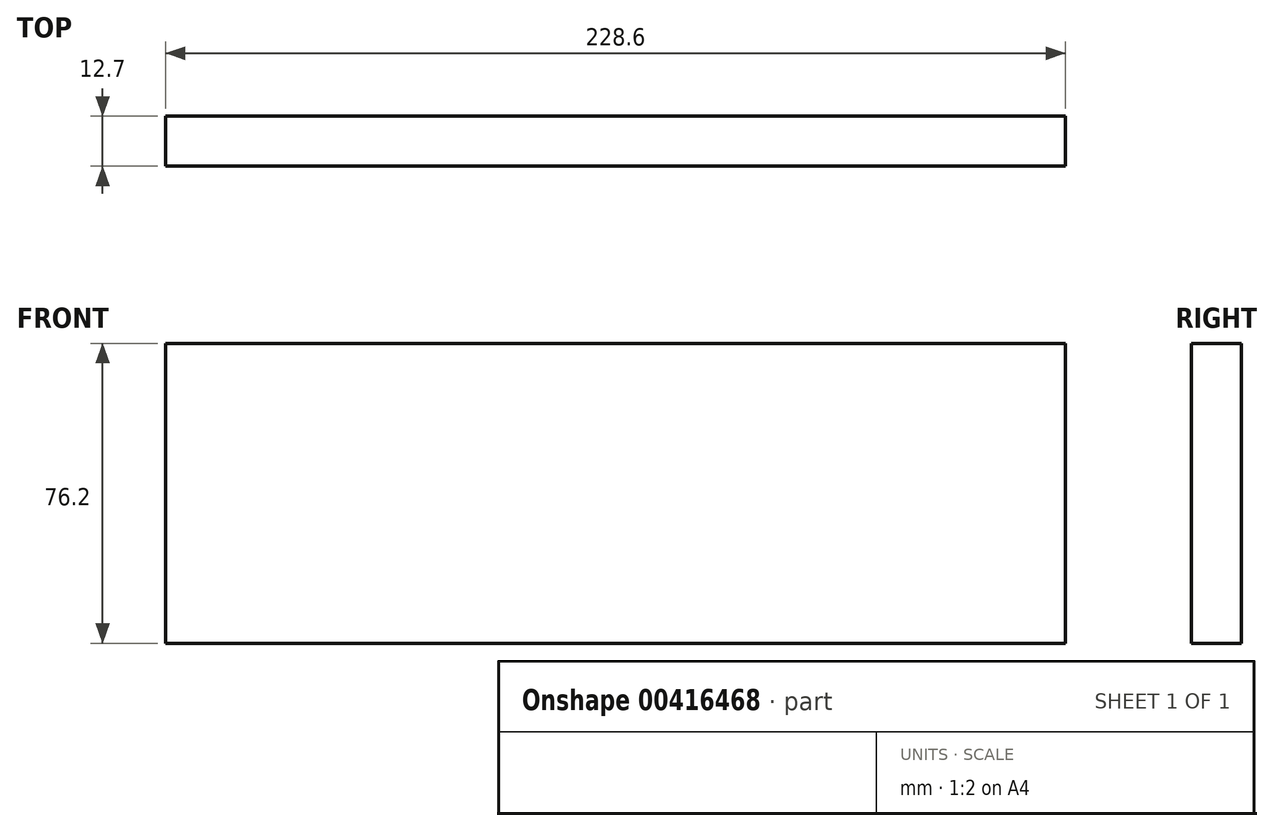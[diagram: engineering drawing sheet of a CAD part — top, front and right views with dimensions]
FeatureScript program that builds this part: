
annotation { "Feature Type Name" : "Feature", "Feature Type Description" : "" }
export const myFeature = defineFeature(function(context is Context, id is Id, definition is map)
    precondition{}
    {
        {
            var Q0;
            Q0=qCreatedBy(makeId("Front.planeOp"),FACE);
            var sketch = newSketch(context, id + "F0", { "sketchPlane" : qUnion([Q0])});
            skLineSegment(sketch, "E0.bottom", {"start": v(-106.74, 30.92) * mm, "end": v(121.86, 30.92) * mm});
            skLineSegment(sketch, "E0.top", {"start": v(-106.74, -45.28) * mm, "end": v(121.86, -45.28) * mm});
            skLineSegment(sketch, "E0.left", {"start": v(-106.74, 30.92) * mm, "end": v(-106.74, -45.28) * mm});
            skLineSegment(sketch, "E0.right", {"start": v(121.86, 30.92) * mm, "end": v(121.86, -45.28) * mm});
            skSolve(sketch);
        }
        {
            var Q0;
            Q0 = qSketchRegion(id + "F0", true);
            extrude(context, id + "F1", {"entities" : qUnion([Q0]), "depth" : 12.7 * mm});
        }
    });
